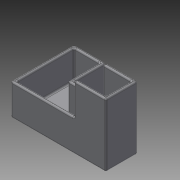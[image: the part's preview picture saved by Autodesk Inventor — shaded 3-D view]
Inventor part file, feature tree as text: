
AUTODESK INVENTOR PART (.ipt)
format: ipt  version: 2014 (Build 180170000, 170)  size: 176,640 bytes
history: native  units: in
note: dims shown in document units (in); Inventor stores cm internally (conversion verified against a paired STEP export)
features: plane x8, extrude x2, other x1, shell x1, fillet x1, sketch x1
ambient origin geometry x8: Origin, YZ Plane, XZ Plane, XY Plane, X Axis, Y Axis, Z Axis, Center Point
bodies: Solid1 (feature_tree)
feature tree (14):
  other  "Cube Master.ipt"
  extrude  "Extrusion1"  Depth=0.3937in
  extrude  "Extrusion2"  Depth=0.0193in TaperAngle=0.0deg
  shell  "Shell1"  Thickness=1.0in
  fillet  "Fillet1"  Radius=0.0394in
  sketch  "Sketch1"  dims[d0=0.3937in d1=0.3937in d2=1.0in d3=0.0in d4=1.0in d5=0.0in d6=0.0394in d7=0.0193in d8=0.0193in]
  plane  "Work Plane1"
  plane  "Work Plane2"
  plane  "Work Plane3"
  plane  "Work Plane4"
  plane  "Work Plane5"
  plane  "Work Plane6"
  plane  "Work Plane7"
  plane  "Work Plane8"
